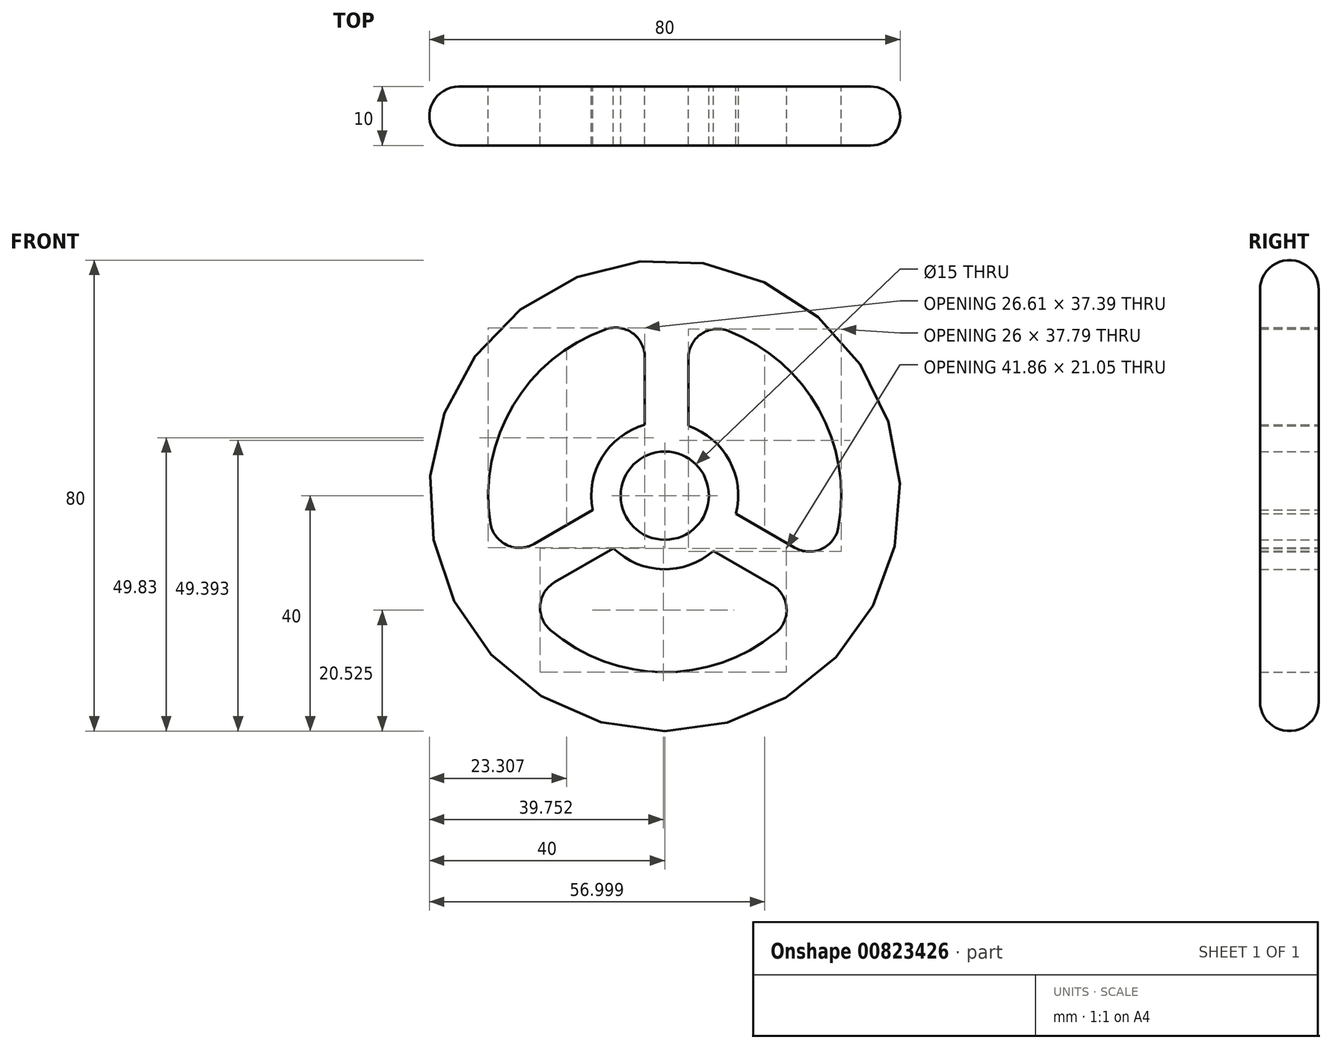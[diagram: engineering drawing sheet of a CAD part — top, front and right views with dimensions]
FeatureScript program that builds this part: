
annotation { "Feature Type Name" : "Feature", "Feature Type Description" : "" }
export const myFeature = defineFeature(function(context is Context, id is Id, definition is map)
    precondition{}
    {
        {
            var Q0;
            Q0=qCreatedBy(makeId("Front.planeOp"),FACE);
            var sketch = newSketch(context, id + "F0", { "sketchPlane" : qUnion([Q0])});
            skCircle(sketch, "E0", {"center": v(0, 0) * mm, "radius": 40 * mm});
            skArc(sketch, "E1", {"start": v(-10.07, 28.26) * mm, "mid": v(-25.78, 15.34) * mm, "end": v(-29.64, -4.64) * mm});
            skCircle(sketch, "E2", {"center": v(0, 0) * mm, "radius": 12.5 * mm});
            skCircle(sketch, "E3", {"center": v(0, 0) * mm, "radius": 7.5 * mm});
            skLineSegment(sketch, "E4.0", {"start": v(-3.4, 40) * mm, "end": v(-3.4, 39.86) * mm});
            skLineSegment(sketch, "E5.0", {"start": v(4, 40) * mm, "end": v(4, 39.8) * mm});
            skLineSegment(sketch, "E6.trimOffspring", {"start": v(-3.4, 23.55) * mm, "end": v(-3.4, 12.03) * mm});
            skLineSegment(sketch, "E7.trimOffspring", {"start": v(4, 23.32) * mm, "end": v(4, 11.84) * mm});
            skPoint(sketch, "E8.orphan", {"position": v(0, 40) * mm});
            skLineSegment(sketch, "E9.1.0", {"start": v(-22.2, -8.2) * mm, "end": v(-12.26, -2.46) * mm});
            skLineSegment(sketch, "E9.1.1", {"start": v(-18.7, -14.71) * mm, "end": v(-8.72, -8.95) * mm});
            skLineSegment(sketch, "E9.2.0", {"start": v(18.2, -15.13) * mm, "end": v(8.26, -9.39) * mm});
            skLineSegment(sketch, "E9.2.1", {"start": v(22.1, -8.84) * mm, "end": v(12.11, -3.08) * mm});
            skArc(sketch, "E10.trimOffspring", {"start": v(-19.44, -22.85) * mm, "mid": v(-0.4, -30) * mm, "end": v(18.84, -23.35) * mm});
            skArc(sketch, "E11.trimOffspring", {"start": v(29.5, -5.41) * mm, "mid": v(26.17, 14.66) * mm, "end": v(10.8, 27.99) * mm});
            skPoint(sketch, "E12.visualSharp", {"position": v(-3.4, 29.8) * mm});
            skArc(sketch, "E12.filletArc", {"start": v(-3.4, 23.55) * mm, "mid": v(-5.5, 27.64) * mm, "end": v(-10.07, 28.26) * mm});
            skPoint(sketch, "E13.visualSharp", {"position": v(4, 29.73) * mm});
            skArc(sketch, "E13.filletArc", {"start": v(10.8, 27.99) * mm, "mid": v(6.17, 27.45) * mm, "end": v(4, 23.32) * mm});
            skPoint(sketch, "E14.visualSharp", {"position": v(27.5, -11.97) * mm});
            skArc(sketch, "E14.filletArc", {"start": v(22.1, -8.84) * mm, "mid": v(26.69, -9.05) * mm, "end": v(29.5, -5.41) * mm});
            skPoint(sketch, "E15.visualSharp", {"position": v(23.75, -18.33) * mm});
            skArc(sketch, "E15.filletArc", {"start": v(18.84, -23.35) * mm, "mid": v(20.68, -19.07) * mm, "end": v(18.2, -15.13) * mm});
            skPoint(sketch, "E16.visualSharp", {"position": v(-24.12, -17.84) * mm});
            skArc(sketch, "E16.filletArc", {"start": v(-18.7, -14.71) * mm, "mid": v(-21.18, -18.59) * mm, "end": v(-19.44, -22.85) * mm});
            skPoint(sketch, "E17.visualSharp", {"position": v(-27.75, -11.4) * mm});
            skArc(sketch, "E17.filletArc", {"start": v(-29.64, -4.64) * mm, "mid": v(-26.86, -8.38) * mm, "end": v(-22.2, -8.2) * mm});
            skSolve(sketch);
        }
        {
            var Q0;
            Q0 = qSketchRegion(id + "F0", true);
            var Q1;
            Q1=makeQuery(id+"F0.imprint","IMPRINT",FACE,{"disambiguationData":[TD([[makeQuery(id+"F0.imprint","IMPRINT",EDGE,{"derivedFrom":sQuery(id+"F0.wireOp",EDGE,"E3")}),-1.0]])]});
            extrude(context, id + "F1", {"entities" : qUnion([Q0, Q1]), "depth" : 10 * mm, "offsetDistance" : 25 * mm});
        }
        {
            var Q0;
            Q0=makeQuery(id+"F1.opExtrude","CAP_EDGE",EDGE,{"disambiguationData":[OSD([sQuery(id+"F0.wireOp",EDGE,"E0")])],"isStart":false});
            var Q1;
            Q1=makeQuery(id+"F1.opExtrude","CAP_EDGE",EDGE,{"disambiguationData":[OSD([sQuery(id+"F0.wireOp",EDGE,"E0")])],"isStart":true});
            fillet(context, id + "F2", {"entities" : qUnion([Q0, Q1]), "radius" : 5 * mm, "tangentPropagation" : true, "allowEdgeOverflow" : false});
        }
    });
